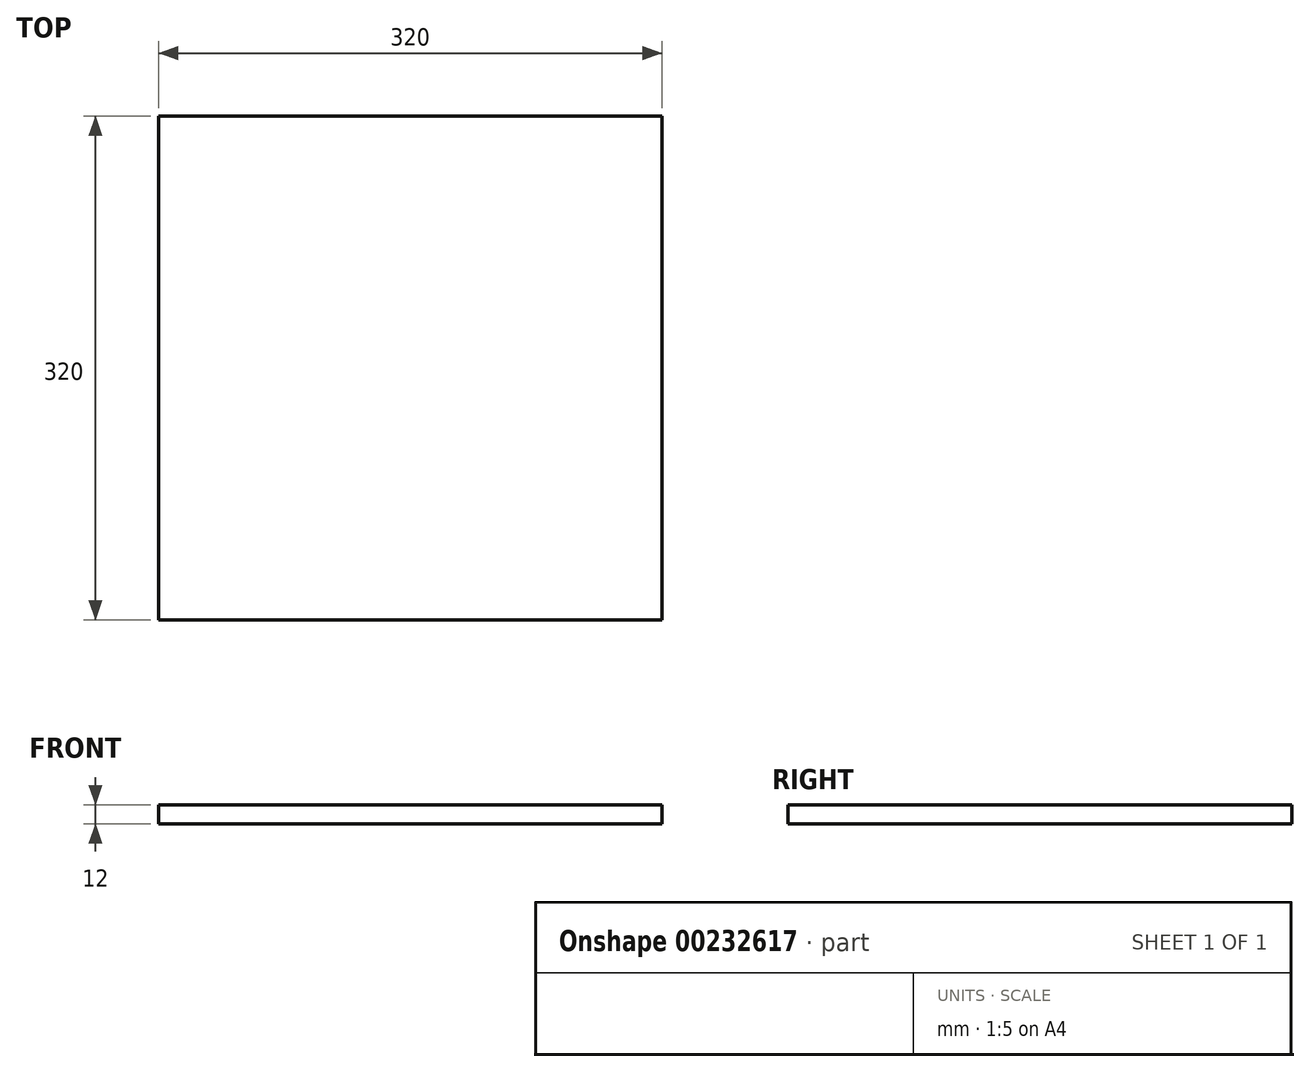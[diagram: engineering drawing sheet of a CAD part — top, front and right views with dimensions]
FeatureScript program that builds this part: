
annotation { "Feature Type Name" : "Feature", "Feature Type Description" : "" }
export const myFeature = defineFeature(function(context is Context, id is Id, definition is map)
    precondition{}
    {
        {
            var Q0;
            Q0=qCreatedBy(makeId("Top.planeOp"),FACE);
            var sketch = newSketch(context, id + "F0", { "sketchPlane" : qUnion([Q0])});
            skLineSegment(sketch, "E0.bottom", {"start": v(0, 0) * mm, "end": v(320, 0) * mm});
            skLineSegment(sketch, "E0.top", {"start": v(0, 320) * mm, "end": v(320, 320) * mm});
            skLineSegment(sketch, "E0.left", {"start": v(0, 0) * mm, "end": v(0, 320) * mm});
            skLineSegment(sketch, "E0.right", {"start": v(320, 0) * mm, "end": v(320, 320) * mm});
            skSolve(sketch);
        }
        {
            var Q0;
            Q0 = qSketchRegion(id + "F0", true);
            extrude(context, id + "F1", {"entities" : qUnion([Q0]), "depth" : 12 * mm});
        }
    });
